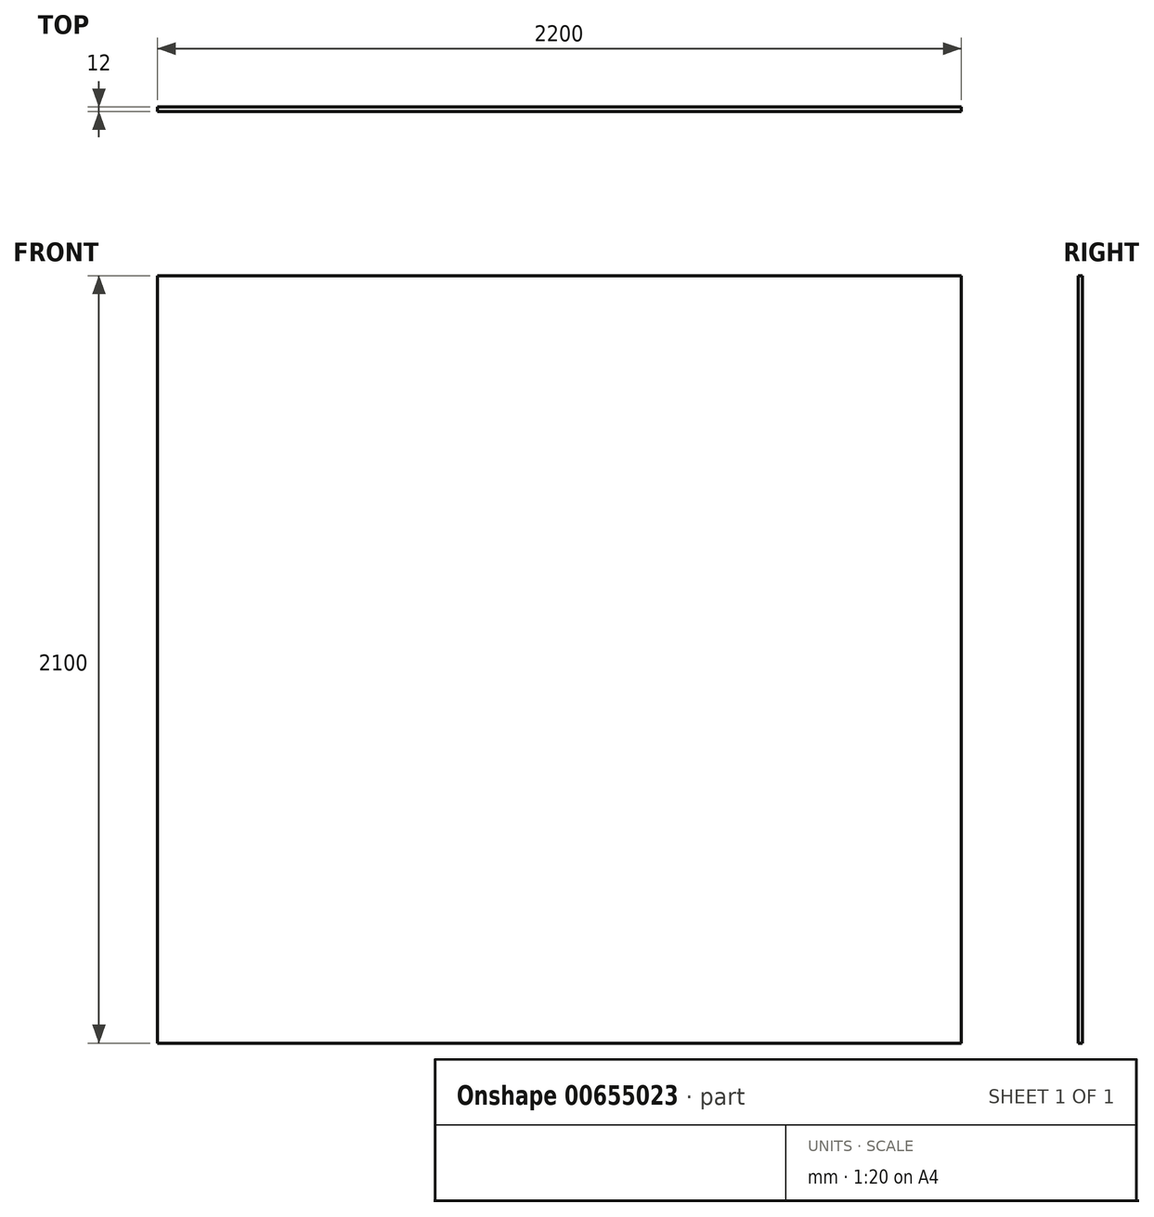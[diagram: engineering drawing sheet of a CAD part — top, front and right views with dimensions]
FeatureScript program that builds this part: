
annotation { "Feature Type Name" : "Feature", "Feature Type Description" : "" }
export const myFeature = defineFeature(function(context is Context, id is Id, definition is map)
    precondition{}
    {
        {
            var Q0;
            Q0=qCreatedBy(makeId("Front.planeOp"),FACE);
            var sketch = newSketch(context, id + "F0", { "sketchPlane" : qUnion([Q0])});
            skLineSegment(sketch, "E0.bottom", {"start": v(1100, -1050) * mm, "end": v(-1100, -1050) * mm});
            skLineSegment(sketch, "E0.top", {"start": v(1100, 1050) * mm, "end": v(-1100, 1050) * mm});
            skLineSegment(sketch, "E0.left", {"start": v(1100, -1050) * mm, "end": v(1100, 1050) * mm});
            skLineSegment(sketch, "E0.right", {"start": v(-1100, -1050) * mm, "end": v(-1100, 1050) * mm});
            skPoint(sketch, "E0.middle", {"position": v(0, 0) * mm});
            skSolve(sketch);
        }
        {
            var Q0;
            Q0 = qSketchRegion(id + "F0", true);
            extrude(context, id + "F1", {"entities" : qUnion([Q0]), "depth" : 12 * mm, "offsetDistance" : 25.4 * mm});
        }
    });
